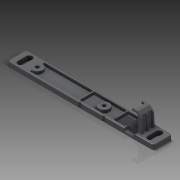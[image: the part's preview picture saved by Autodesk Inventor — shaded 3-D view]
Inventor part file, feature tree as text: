
AUTODESK INVENTOR PART (.ipt)
format: ipt  version: 2011 (Build 150239000, 239)  size: 385,024 bytes
history: native  units: in
note: dims shown in document units (in); Inventor stores cm internally (conversion verified against a paired STEP export)
features: fillet x1, imported_body x1
ambient origin geometry x8: Origin, YZ Plane, XZ Plane, XY Plane, X Axis, Y Axis, Z Axis, Center Point
feature tree (2):
  fillet  "Fillet8"  [1 undecoded]
  imported_body  "Base1"
note: 1 required parameter value undecoded (feature->parameter linkage not recoverable at this tier; creation-order binding heuristic only, values carry confidence <= 0.55)
